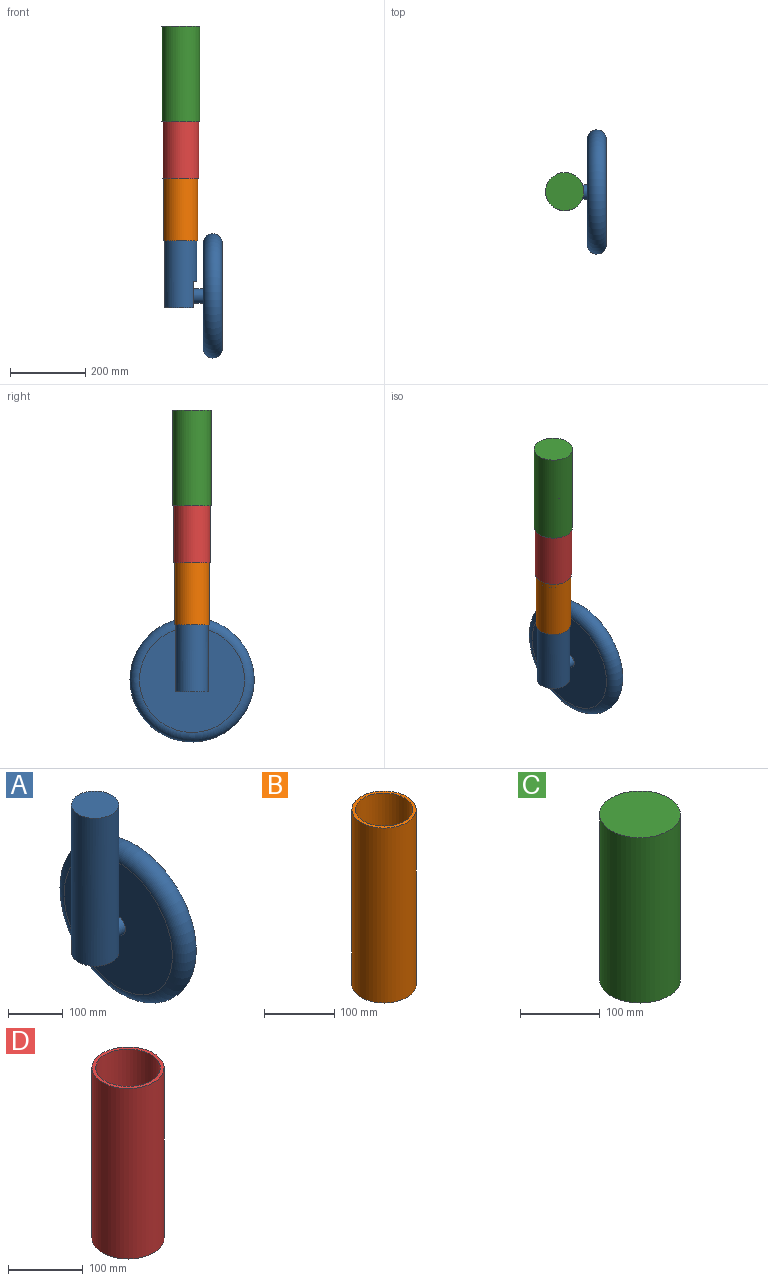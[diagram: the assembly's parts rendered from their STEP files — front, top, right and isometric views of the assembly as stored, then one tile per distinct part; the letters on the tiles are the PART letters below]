
ASSEMBLY  parts=4 mates=3
PART A: 9 faces, bbox 153.6x357.4x477.2 mm
  f0: cylinder r=19.05mm len=38.1mm, axis (-1,0,0), area 3040.2mm2, adj f4,f6
  f1: cylinder r=43.18mm len=330.2mm, axis (0,0,-1), area 85568.2mm2, adj f2,f3,f4,f5
  f2: plane 86.36x86.36mm, normal (0,0,1), area 5857.5mm2, adj f1
  f3: plane 86.36x77.45mm, normal (0,0,-1), area 5538.2mm2, adj f1,f4
  f4: plane 71.12x52.55mm, normal (1,0,0), area 2597.1mm2, adj f0,f1,f3,f5
  f5: plane 52.55x8.91mm, normal (0,0,-1), area 319.3mm2, adj f1,f4
  f6: plane 279.4x279.4mm, normal (-1,0,0), area 60171.5mm2, adj f0,f8
  f7: plane 279.4x279.4mm, normal (1,0,0), area 61311.6mm2, adj f8
  f8: torus R=139.7mm, axis (1,0,0), area 78149.5mm2, adj f6,f7
PART B: 4 faces, bbox 91.4x91.4x304.8 mm
  f0: cylinder r=45.72mm len=304.8mm, axis (0,0,-1), area 87559.1mm2, adj f1,f2
  f1: plane 91.44x91.44mm, normal (0,0,1), area 1378.2mm2, adj f0,f3
  f2: plane 91.44x91.44mm, normal (0,0,-1), area 1378.2mm2, adj f0,f3
  f3: cylinder r=40.64mm len=304.8mm, axis (0,0,-1), area 77830.3mm2, adj f1,f2
PART C: 5 faces, bbox 101.6x101.6x254 mm
  f0: cylinder r=50.8mm len=254mm, axis (0,0,-1), area 81073.2mm2, adj f1,f2
  f1: plane 101.6x101.6mm, normal (0,0,1), area 8107.3mm2, adj f0
  f2: plane 101.6x101.6mm, normal (0,0,-1), area 1540.4mm2, adj f0,f3
  f3: cylinder r=45.72mm len=248.92mm, axis (0,0,-1), area 71506.6mm2, adj f2,f4
  f4: plane 91.44x91.44mm, normal (0,0,-1), area 6566.9mm2, adj f3
PART D: 4 faces, bbox 96.5x96.5x279.4 mm
  f0: cylinder r=48.26mm len=279.4mm, axis (0,0,-1), area 84721.5mm2, adj f1,f2
  f1: plane 96.52x96.52mm, normal (0,0,1), area 1459.3mm2, adj f0,f3
  f2: plane 96.52x96.52mm, normal (0,0,-1), area 1459.3mm2, adj f0,f3
  f3: cylinder r=43.18mm len=279.4mm, axis (0,0,-1), area 75803.4mm2, adj f1,f2
PLACE A t=(0,0,-495.3)mm
PLACE B t=(0,0,-317.5)mm
PLACE C at identity
PLACE D t=(0,0,-152.4)mm
MATE fastened D.f0 <-> C.f0  axis (0,0,-1) through (0,0,127)mm
MATE fastened A.f1 <-> B.f0  axis (0,0,1) through (0,0,-165.1)mm
MATE fastened B.f0 <-> D.f0  axis (0,0,-1) through (0,0,-12.7)mm
